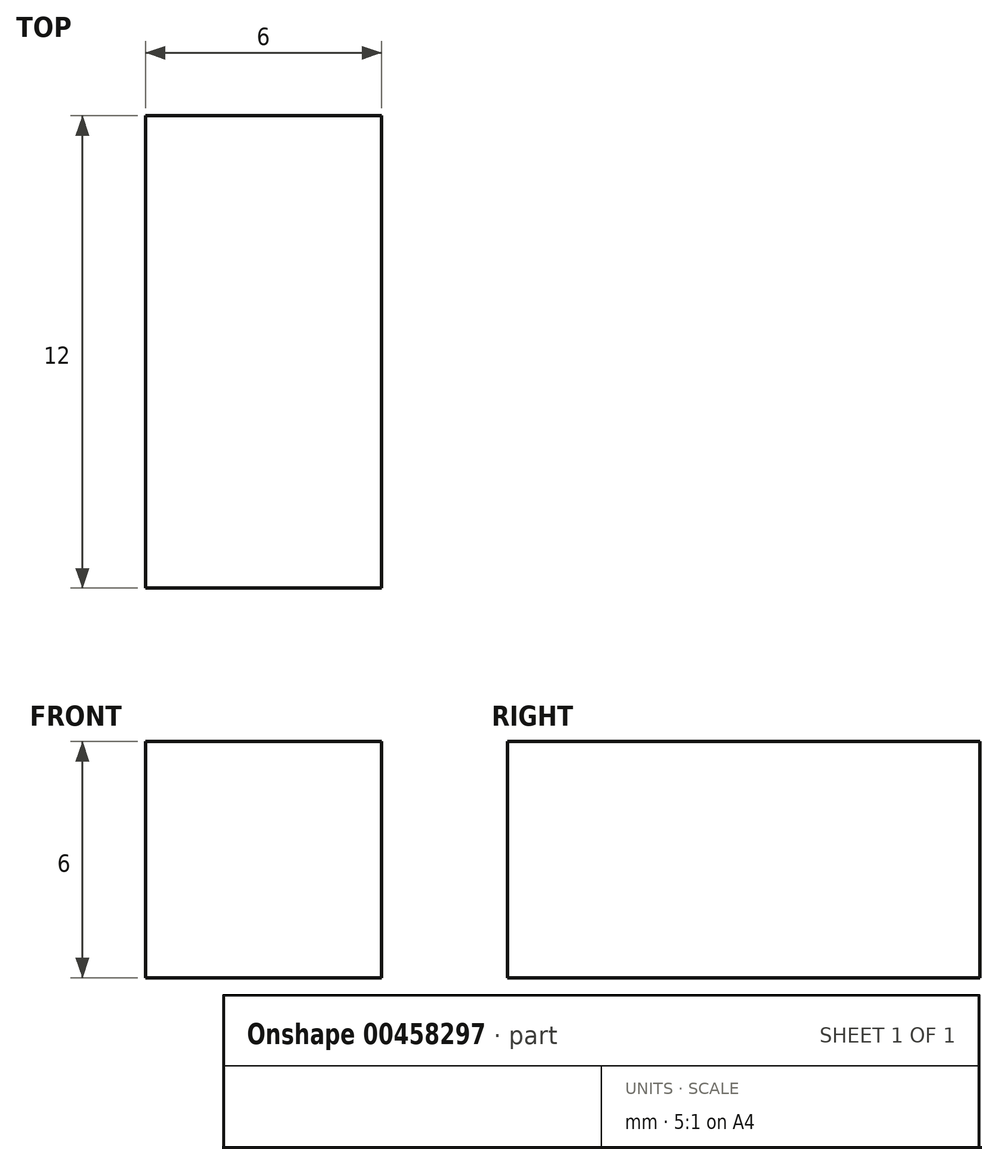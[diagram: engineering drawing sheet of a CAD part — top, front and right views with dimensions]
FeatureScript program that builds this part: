
annotation { "Feature Type Name" : "Feature", "Feature Type Description" : "" }
export const myFeature = defineFeature(function(context is Context, id is Id, definition is map)
    precondition{}
    {
        {
            var Q0;
            Q0=qCreatedBy(makeId("Front.planeOp"),FACE);
            var sketch = newSketch(context, id + "F0", { "sketchPlane" : qUnion([Q0])});
            skLineSegment(sketch, "E0.bottom", {"start": v(0, 0) * mm, "end": v(-6, 0) * mm});
            skLineSegment(sketch, "E0.top", {"start": v(0, 6) * mm, "end": v(-6, 6) * mm});
            skLineSegment(sketch, "E0.left", {"start": v(0, 0) * mm, "end": v(0, 6) * mm});
            skLineSegment(sketch, "E0.right", {"start": v(-6, 0) * mm, "end": v(-6, 6) * mm});
            skSolve(sketch);
        }
        {
            var Q0;
            Q0=makeQuery(id+"F0.imprint","IMPRINT",FACE,{"disambiguationData":[TD([[makeQuery(id+"F0.imprint","IMPRINT",EDGE,{"derivedFrom":sQuery(id+"F0.wireOp",EDGE,"E0.bottom")}),-1.0]])]});
            extrude(context, id + "F1", {"entities" : qUnion([Q0]), "depth" : 12 * mm});
        }
    });
